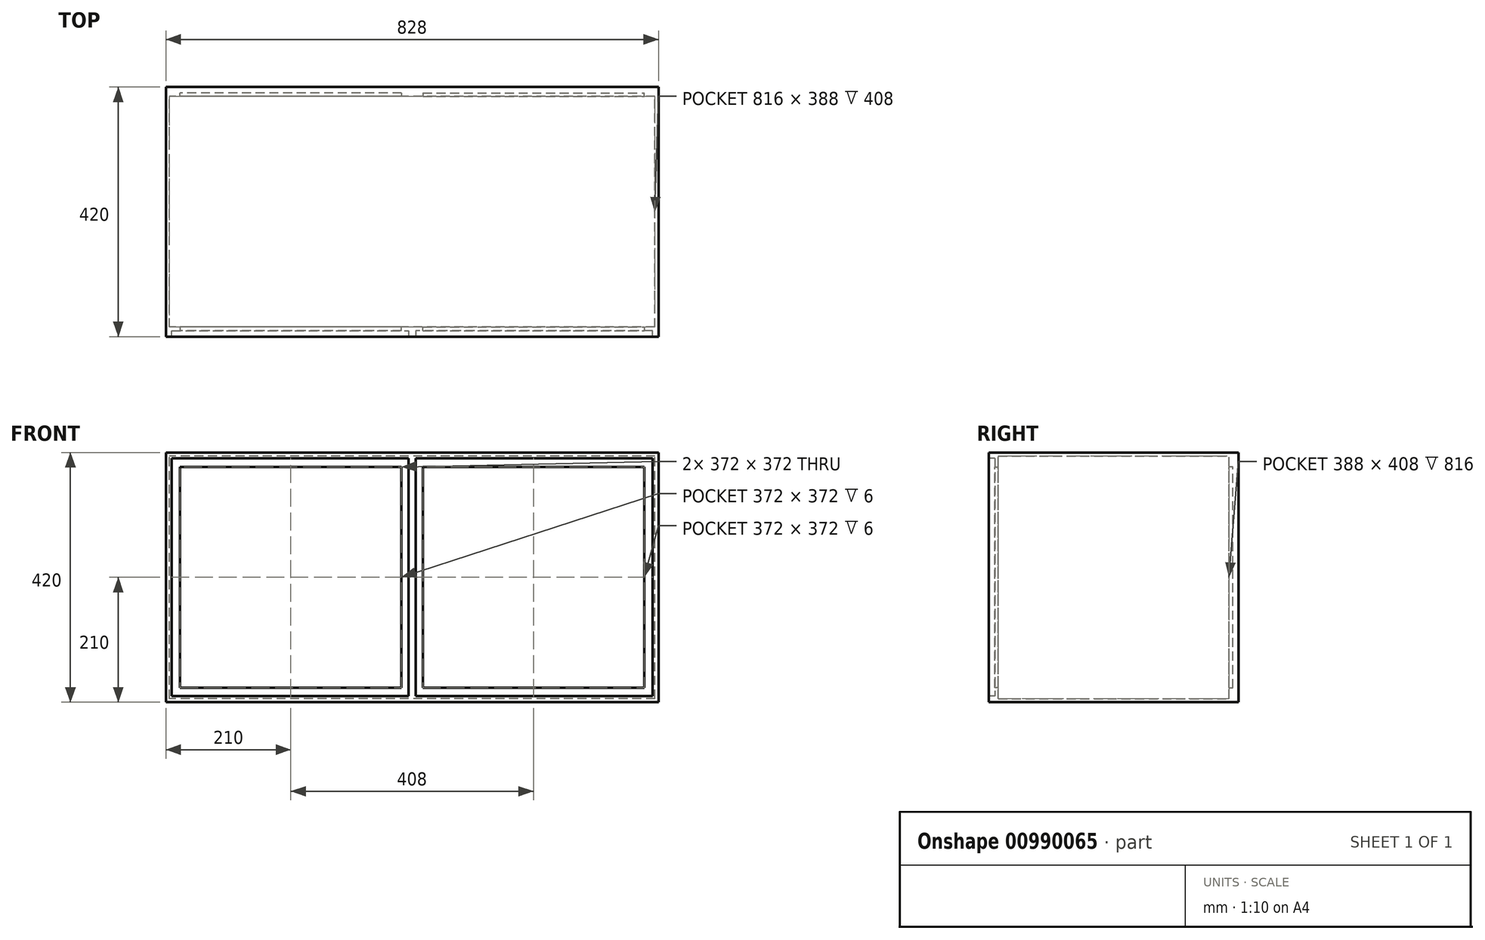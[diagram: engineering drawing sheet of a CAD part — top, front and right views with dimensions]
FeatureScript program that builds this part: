
annotation { "Feature Type Name" : "Feature", "Feature Type Description" : "" }
export const myFeature = defineFeature(function(context is Context, id is Id, definition is map)
    precondition{}
    {
        {
            var Q0;
            Q0=qCreatedBy(makeId("Front.planeOp"),FACE);
            var sketch = newSketch(context, id + "F0", { "sketchPlane" : qUnion([Q0])});
            skLineSegment(sketch, "E0.bottom", {"start": v(-210, 210) * mm, "end": v(210, 210) * mm});
            skLineSegment(sketch, "E0.top", {"start": v(-210, -210) * mm, "end": v(210, -210) * mm});
            skLineSegment(sketch, "E0.left", {"start": v(-210, 210) * mm, "end": v(-210, -210) * mm});
            skLineSegment(sketch, "E0.right", {"start": v(210, 210) * mm, "end": v(210, -210) * mm});
            skPoint(sketch, "E0.middle", {"position": v(0, 0) * mm});
            skSolve(sketch);
        }
        {
            var Q0;
            Q0=qSketchRegion(id+"F0",true);
            extrude(context, id + "F1", {"entities" : qUnion([Q0]), "endBound" : BoundingType.SYMMETRIC, "depth" : 210 * mm, "offsetDistance" : 25.4 * mm});
        }
        {
            var Q0;
            Q0=makeQuery(id+"F1.opExtrude","CAP_FACE",FACE,{"disambiguationData":[OSD([sQuery(id+"F0.wireOp",EDGE,"E0.bottom"),sQuery(id+"F0.wireOp",EDGE,"E0.top"),sQuery(id+"F0.wireOp",EDGE,"E0.left"),sQuery(id+"F0.wireOp",EDGE,"E0.right")])],"isStart":false});
            shell(context, id + "F2", {"entities" : qUnion([Q0]), "thickness" : 6 * mm});
        }
        {
            var Q0;
            Q0=makeQuery(id+"F2.opShell","OFFSET_FACE",FACE,{"disambiguationData":[OSD([sQuery(id+"F0.wireOp",EDGE,"E0.left")])]});
            var sketch = newSketch(context, id + "F3", { "sketchPlane" : qUnion([Q0])});
            skLineSegment(sketch, "E1.top", {"start": v(-2, -194) * mm, "end": v(2, -194) * mm});
            skPoint(sketch, "E1.middle", {"position": v(0, 0) * mm});
            skLineSegment(sketch, "E2.bottom", {"start": v(-89, -204) * mm, "end": v(-95, -204) * mm});
            skLineSegment(sketch, "E2.top", {"start": v(-89, 204) * mm, "end": v(-95, 204) * mm});
            skLineSegment(sketch, "E2.left", {"start": v(-89, -204) * mm, "end": v(-89, 204) * mm});
            skLineSegment(sketch, "E2.right", {"start": v(-95, -204) * mm, "end": v(-95, 204) * mm});
            skPoint(sketch, "E2.middle", {"position": v(-92, 0) * mm});
            skSolve(sketch);
        }
        {
            var Q0;
            Q0=qSketchRegion(id+"F3",true);
            extrude(context, id + "F4", {"entities" : qUnion([Q0]), "operationType" : NewBodyOperationType.ADD, "depth" : 18 * mm, "offsetDistance" : 25.4 * mm});
        }
        {
            var Q0;
            Q0=makeQuery(id+"F2.opShell","OFFSET_FACE",FACE,{"disambiguationData":[OSD([sQuery(id+"F0.wireOp",EDGE,"E0.right")])]});
            var sketch = newSketch(context, id + "F5", { "sketchPlane" : qUnion([Q0])});
            skLineSegment(sketch, "E3.bottom", {"start": v(95, -204) * mm, "end": v(89, -204) * mm});
            skLineSegment(sketch, "E3.top", {"start": v(95, 204) * mm, "end": v(89, 204) * mm});
            skLineSegment(sketch, "E3.left", {"start": v(89, -204) * mm, "end": v(89, 204) * mm});
            skLineSegment(sketch, "E3.right", {"start": v(95, -204) * mm, "end": v(95, 204) * mm});
            skPoint(sketch, "E3.middle", {"position": v(92, 0) * mm});
            skSolve(sketch);
        }
        {
            var Q0;
            Q0=qSketchRegion(id+"F5",true);
            extrude(context, id + "F6", {"entities" : qUnion([Q0]), "operationType" : NewBodyOperationType.ADD, "depth" : 18 * mm, "offsetDistance" : 25.4 * mm});
        }
        {
            var Q0;
            Q0=makeQuery(id+"F4.opExtrude","CAP_FACE",FACE,{"disambiguationData":[OSD([sQuery(id+"F3.wireOp",EDGE,"E2.bottom"),sQuery(id+"F3.wireOp",EDGE,"E2.top"),sQuery(id+"F3.wireOp",EDGE,"E2.left"),sQuery(id+"F3.wireOp",EDGE,"E2.right")])],"isStart":false});
            var sketch = newSketch(context, id + "F7", { "sketchPlane" : qUnion([Q0])});
            skLineSegment(sketch, "E4.bottom", {"start": v(-95, 204) * mm, "end": v(-89, 204) * mm});
            skLineSegment(sketch, "E4.top", {"start": v(-95, 186) * mm, "end": v(-89, 186) * mm});
            skLineSegment(sketch, "E4.left", {"start": v(-95, 204) * mm, "end": v(-95, 186) * mm});
            skLineSegment(sketch, "E4.right", {"start": v(-89, 204) * mm, "end": v(-89, 186) * mm});
            skSolve(sketch);
        }
        {
            var Q0;
            Q0=qSketchRegion(id+"F7",true);
            var Q1;
            Q1=makeQuery(id+"F6.opExtrude","CAP_FACE",FACE,{"disambiguationData":[OSD([sQuery(id+"F5.wireOp",EDGE,"E3.bottom"),sQuery(id+"F5.wireOp",EDGE,"E3.top"),sQuery(id+"F5.wireOp",EDGE,"E3.left"),sQuery(id+"F5.wireOp",EDGE,"E3.right")])],"isStart":false});
            extrude(context, id + "F8", {"entities" : qUnion([Q0]), "operationType" : NewBodyOperationType.ADD, "endBound" : BoundingType.UP_TO_SURFACE, "depth" : 12.2 * mm, "endBoundEntityFace" : qUnion([Q1]), "offsetDistance" : 25.4 * mm});
        }
        {
            var Q0;
            Q0=makeQuery(id+"F4.opExtrude","CAP_FACE",FACE,{"disambiguationData":[OSD([sQuery(id+"F3.wireOp",EDGE,"E2.bottom"),sQuery(id+"F3.wireOp",EDGE,"E2.top"),sQuery(id+"F3.wireOp",EDGE,"E2.left"),sQuery(id+"F3.wireOp",EDGE,"E2.right")])],"isStart":false});
            var sketch = newSketch(context, id + "F9", { "sketchPlane" : qUnion([Q0])});
            skLineSegment(sketch, "E5.bottom", {"start": v(-89, -204) * mm, "end": v(-95, -204) * mm});
            skLineSegment(sketch, "E5.top", {"start": v(-89, -186) * mm, "end": v(-95, -186) * mm});
            skLineSegment(sketch, "E5.left", {"start": v(-89, -204) * mm, "end": v(-89, -186) * mm});
            skLineSegment(sketch, "E5.right", {"start": v(-95, -204) * mm, "end": v(-95, -186) * mm});
            skSolve(sketch);
        }
        {
            var Q0;
            Q0=qSketchRegion(id+"F9",true);
            var Q1;
            Q1=makeQuery(id+"F6.opExtrude","CAP_FACE",FACE,{"disambiguationData":[OSD([sQuery(id+"F5.wireOp",EDGE,"E3.bottom"),sQuery(id+"F5.wireOp",EDGE,"E3.top"),sQuery(id+"F5.wireOp",EDGE,"E3.left"),sQuery(id+"F5.wireOp",EDGE,"E3.right")])],"isStart":false});
            extrude(context, id + "F10", {"entities" : qUnion([Q0]), "operationType" : NewBodyOperationType.ADD, "endBound" : BoundingType.UP_TO_SURFACE, "depth" : 25.4 * mm, "endBoundEntityFace" : qUnion([Q1]), "offsetDistance" : 25.4 * mm});
        }
        {
            var Q0;
            Q0=makeQuery(id+"F10.boolean.opBoolean","MERGE",FACE,{"derivedFrom":[makeQuery(id+"F8.boolean.opBoolean","MERGE",FACE,{"derivedFrom":[makeQuery(id+"F4.opExtrude","SWEPT_FACE",FACE,{"disambiguationData":[OSD([sQuery(id+"F3.wireOp",EDGE,"E2.right")])]}),makeQuery(id+"F6.opExtrude","SWEPT_FACE",FACE,{"disambiguationData":[OSD([sQuery(id+"F5.wireOp",EDGE,"E3.right")])]}),makeQuery(id+"F8.opExtrude","SWEPT_FACE",FACE,{"disambiguationData":[OSD([sQuery(id+"F7.wireOp",EDGE,"E4.left")])]})]}),makeQuery(id+"F10.opExtrude","SWEPT_FACE",FACE,{"disambiguationData":[OSD([sQuery(id+"F9.wireOp",EDGE,"E5.right")])]})]});
            var sketch = newSketch(context, id + "F11", { "sketchPlane" : qUnion([Q0])});
            skLineSegment(sketch, "E6.bottom", {"start": v(-204, 204) * mm, "end": v(204, 204) * mm});
            skLineSegment(sketch, "E6.top", {"start": v(-204, -204) * mm, "end": v(204, -204) * mm});
            skLineSegment(sketch, "E6.left", {"start": v(-204, 204) * mm, "end": v(-204, -204) * mm});
            skLineSegment(sketch, "E6.right", {"start": v(204, 204) * mm, "end": v(204, -204) * mm});
            skPoint(sketch, "E6.middle", {"position": v(0, 0) * mm});
            skLineSegment(sketch, "E7.bottom", {"start": v(-200, 200) * mm, "end": v(200, 200) * mm});
            skLineSegment(sketch, "E7.top", {"start": v(-200, -200) * mm, "end": v(200, -200) * mm});
            skLineSegment(sketch, "E7.left", {"start": v(-200, 200) * mm, "end": v(-200, -200) * mm});
            skLineSegment(sketch, "E7.right", {"start": v(200, 200) * mm, "end": v(200, -200) * mm});
            skSolve(sketch);
        }
        {
            var Q0;
            Q0=qSketchRegion(id+"F11",true);
            extrude(context, id + "F12", {"entities" : qUnion([Q0]), "operationType" : NewBodyOperationType.ADD, "depth" : 10 * mm, "offsetDistance" : 25.4 * mm});
        }
        {
            var Q0;
            Q0=makeQuery(id+"F1.opExtrude","SWEPT_BODY",BODY,{"disambiguationData":[OSD([sQuery(id+"F0.wireOp",EDGE,"E0.bottom"),sQuery(id+"F0.wireOp",EDGE,"E0.top"),sQuery(id+"F0.wireOp",EDGE,"E0.left"),sQuery(id+"F0.wireOp",EDGE,"E0.right")])]});
            var Q1;
            Q1=makeQuery(id+"F1.opExtrude","CAP_FACE",FACE,{"disambiguationData":[OSD([sQuery(id+"F0.wireOp",EDGE,"E0.bottom"),sQuery(id+"F0.wireOp",EDGE,"E0.top"),sQuery(id+"F0.wireOp",EDGE,"E0.left"),sQuery(id+"F0.wireOp",EDGE,"E0.right")])],"isStart":true});
            mirror(context, id + "F13", {"operationType" : NewBodyOperationType.ADD, "entities" : qUnion([Q0]), "mirrorPlane" : qUnion([Q1])});
        }
        {
            var Q0;
            Q0=makeQuery(id+"F13.opPattern","COPY",FACE,{"derivedFrom":makeQuery(id+"F2.opShell","OFFSET_FACE",FACE,{"disambiguationData":[OSD([sQuery(id+"F0.wireOp",EDGE,"E0.bottom"),sQuery(id+"F0.wireOp",EDGE,"E0.top"),sQuery(id+"F0.wireOp",EDGE,"E0.left"),sQuery(id+"F0.wireOp",EDGE,"E0.right")])]}),"instanceName":"1"});
            extrude(context, id + "F14", {"entities" : qUnion([Q0]), "operationType" : NewBodyOperationType.REMOVE, "oppositeDirection" : true, "depth" : 25.4 * mm, "offsetDistance" : 25.4 * mm});
        }
        {
            var Q0;
            Q0=makeQuery(id+"F13.opPattern","COPY",FACE,{"derivedFrom":makeQuery(id+"F10.boolean.opBoolean","MERGE",FACE,{"derivedFrom":[makeQuery(id+"F8.boolean.opBoolean","MERGE",FACE,{"derivedFrom":[makeQuery(id+"F4.opExtrude","SWEPT_FACE",FACE,{"disambiguationData":[OSD([sQuery(id+"F3.wireOp",EDGE,"E2.right")])]}),makeQuery(id+"F6.opExtrude","SWEPT_FACE",FACE,{"disambiguationData":[OSD([sQuery(id+"F5.wireOp",EDGE,"E3.right")])]}),makeQuery(id+"F8.opExtrude","SWEPT_FACE",FACE,{"disambiguationData":[OSD([sQuery(id+"F7.wireOp",EDGE,"E4.left")])]})]}),makeQuery(id+"F10.opExtrude","SWEPT_FACE",FACE,{"disambiguationData":[OSD([sQuery(id+"F9.wireOp",EDGE,"E5.right")])]})]}),"instanceName":"1"});
            var sketch = newSketch(context, id + "F15", { "sketchPlane" : qUnion([Q0])});
            skLineSegment(sketch, "E8.bottom", {"start": v(-200, 200) * mm, "end": v(200, 200) * mm});
            skLineSegment(sketch, "E8.top", {"start": v(-200, -200) * mm, "end": v(200, -200) * mm});
            skLineSegment(sketch, "E8.left", {"start": v(-200, 200) * mm, "end": v(-200, -200) * mm});
            skLineSegment(sketch, "E8.right", {"start": v(200, 200) * mm, "end": v(200, -200) * mm});
            skPoint(sketch, "E8.middle", {"position": v(0, 0) * mm});
            skSolve(sketch);
        }
        {
            var Q0;
            Q0=qSketchRegion(id+"F15",true);
            extrude(context, id + "F16", {"entities" : qUnion([Q0]), "operationType" : NewBodyOperationType.ADD, "depth" : 10 * mm, "offsetDistance" : 25.4 * mm});
        }
        {
            var Q0;
            Q0=makeQuery(id+"F1.opExtrude","SWEPT_BODY",BODY,{"disambiguationData":[OSD([sQuery(id+"F0.wireOp",EDGE,"E0.bottom"),sQuery(id+"F0.wireOp",EDGE,"E0.top"),sQuery(id+"F0.wireOp",EDGE,"E0.left"),sQuery(id+"F0.wireOp",EDGE,"E0.right")])]});
            var Q1;
            {var subQ0=sQuery(id+"F0.wireOp",EDGE,"E0.right");var subQ3=makeQuery(id+"F6.boolean.opBoolean","SPLIT",FACE,{"disambiguationData":[TD([makeQuery(id+"F6.opExtrude","SWEPT_FACE",FACE,{"disambiguationData":[OSD([sQuery(id+"F5.wireOp",EDGE,"E3.left")])]})])],"derivedFrom":makeQuery(id+"F2.opShell","OFFSET_FACE",FACE,{"disambiguationData":[OSD([subQ0])]})});Q1=makeQuery(id+"F14.boolean.opBoolean","MERGE",FACE,{"derivedFrom":[subQ3,makeQuery(id+"F13.opPattern","COPY",FACE,{"derivedFrom":subQ3,"instanceName":"1"})],"fromTools":[makeQuery(id+"F14.opExtrude","SWEPT_FACE",FACE,{"disambiguationData":[OSD([subQ0])]})]});}
            mirror(context, id + "F17", {"operationType" : NewBodyOperationType.ADD, "entities" : qUnion([Q0]), "mirrorPlane" : qUnion([Q1])});
        }
        {
            var Q0;
            {var subQ3=sQuery(id+"F0.wireOp",EDGE,"E0.right");var subQ8=sQuery(id+"F0.wireOp",EDGE,"E0.bottom");var subQ12=makeQuery(id+"F2.opShell","OFFSET_FACE",FACE,{"disambiguationData":[OSD([subQ8])]});var subQ13=makeQuery(id+"F1.opExtrude","SWEPT_FACE",FACE,{"disambiguationData":[OSD([subQ3])]});Q0=makeQuery(id+"F17.boolean.opBoolean","SPLIT",FACE,{"disambiguationData":[TD([subQ12])],"derivedFrom":makeQuery(id+"F17.opPattern","COPY",FACE,{"derivedFrom":makeQuery(id+"F13.boolean.opBoolean","MERGE",FACE,{"derivedFrom":[subQ13,makeQuery(id+"F13.opPattern","COPY",FACE,{"derivedFrom":subQ13,"instanceName":"1"})]}),"instanceName":"1"})});}
            extrude(context, id + "F18", {"entities" : qUnion([Q0]), "operationType" : NewBodyOperationType.REMOVE, "oppositeDirection" : true, "depth" : 25.4 * mm, "offsetDistance" : 25.4 * mm});
        }
    });
